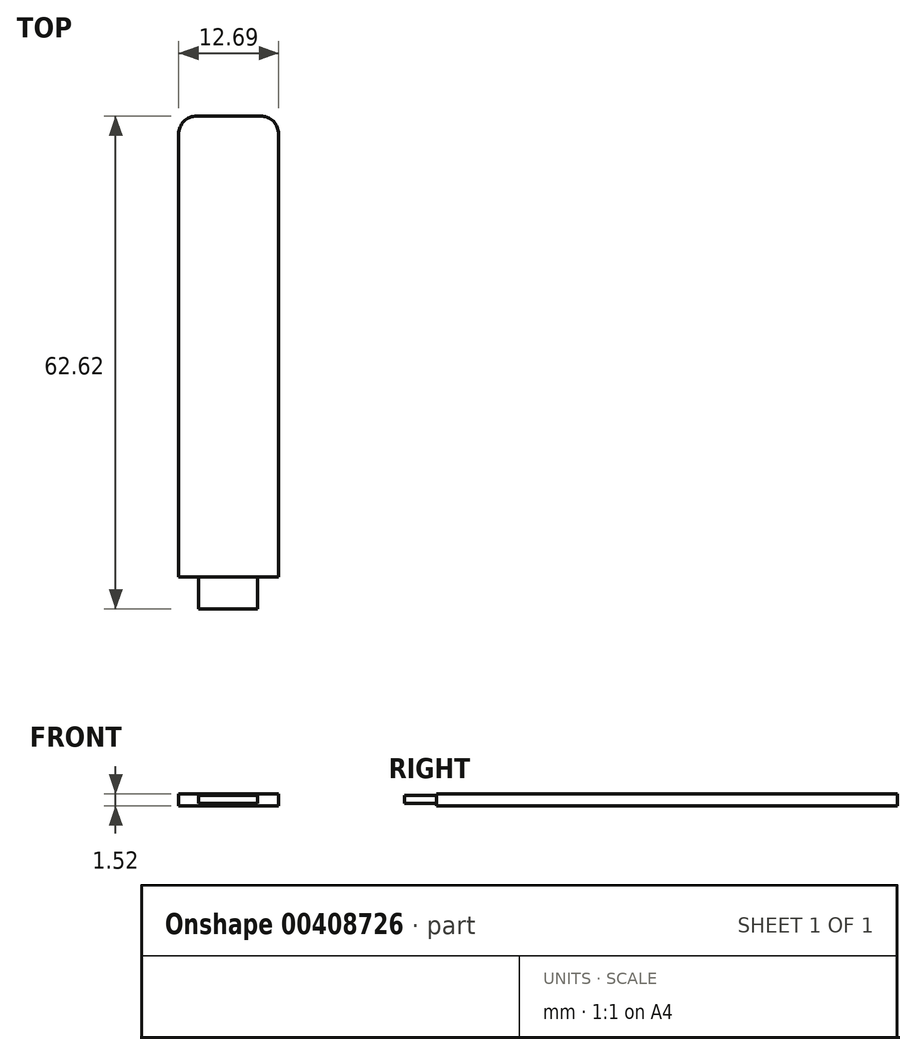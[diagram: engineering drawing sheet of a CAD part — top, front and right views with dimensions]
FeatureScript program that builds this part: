
annotation { "Feature Type Name" : "Feature", "Feature Type Description" : "" }
export const myFeature = defineFeature(function(context is Context, id is Id, definition is map)
    precondition{}
    {
        {
            var Q0;
            Q0=qCreatedBy(makeId("Top.planeOp"),FACE);
            var sketch = newSketch(context, id + "F0", { "sketchPlane" : qUnion([Q0])});
            skLineSegment(sketch, "E0.bottom", {"start": v(-6.25, -9) * mm, "end": v(6.44, -9) * mm});
            skLineSegment(sketch, "E0.top", {"start": v(-6.25, 49.56) * mm, "end": v(6.44, 49.56) * mm});
            skLineSegment(sketch, "E0.left", {"start": v(-6.25, -9) * mm, "end": v(-6.25, 49.56) * mm});
            skLineSegment(sketch, "E0.right", {"start": v(6.44, -9) * mm, "end": v(6.44, 49.56) * mm});
            skLineSegment(sketch, "E1.bottom", {"start": v(-4.3, -9) * mm, "end": v(4.51, -9) * mm});
            skLineSegment(sketch, "E1.top", {"start": v(-4.3, -13.2) * mm, "end": v(4.51, -13.2) * mm});
            skLineSegment(sketch, "E1.left", {"start": v(-4.3, -9) * mm, "end": v(-4.3, -13.2) * mm});
            skLineSegment(sketch, "E1.right", {"start": v(4.51, -9) * mm, "end": v(4.51, -13.2) * mm});
            skSolve(sketch);
        }
        {
            var Q0;
            Q0=makeQuery(id+"F0.imprint","IMPRINT",FACE,{"disambiguationData":[TD([[makeQuery(id+"F0.imprint","IMPRINT",EDGE,{"derivedFrom":sQuery(id+"F0.wireOp",EDGE,"E0.top")}),-1.0]])]});
            extrude(context, id + "F1", {"entities" : qUnion([Q0]), "depth" : 1.52 * mm});
        }
        {
            var Q0;
            Q0=makeQuery(id+"F1.opExtrude","SWEPT_EDGE",EDGE,{"disambiguationData":[OSD([sQuery(id+"F0.wireOp",EDGE,"E0.top"),sQuery(id+"F0.wireOp",EDGE,"E0.left")])]});
            var Q1;
            Q1=makeQuery(id+"F1.opExtrude","SWEPT_EDGE",EDGE,{"disambiguationData":[OSD([sQuery(id+"F0.wireOp",EDGE,"E0.top"),sQuery(id+"F0.wireOp",EDGE,"E0.right")])]});
            fillet(context, id + "F2", {"entities" : qUnion([Q0, Q1]), "radius" : 2.3 * mm, "tangentPropagation" : true, "allowEdgeOverflow" : false});
        }
        {
            var Q0;
            Q0=makeQuery(id+"F1.opExtrude","SWEPT_FACE",FACE,{"disambiguationData":[OSD([sQuery(id+"F0.wireOp",EDGE,"E0.bottom"),sQuery(id+"F0.wireOp",EDGE,"E1.bottom")])]});
            var sketch = newSketch(context, id + "F3", { "sketchPlane" : qUnion([Q0])});
            skLineSegment(sketch, "E2.bottom", {"start": v(3.75, 1.35) * mm, "end": v(-3.75, 1.35) * mm});
            skLineSegment(sketch, "E2.top", {"start": v(3.75, 0.3) * mm, "end": v(-3.75, 0.3) * mm});
            skLineSegment(sketch, "E2.left", {"start": v(3.75, 1.35) * mm, "end": v(3.75, 0.3) * mm});
            skLineSegment(sketch, "E2.right", {"start": v(-3.75, 1.35) * mm, "end": v(-3.75, 0.3) * mm});
            skPoint(sketch, "E2.middle", {"position": v(0, 0.82) * mm});
            skSolve(sketch);
        }
        {
            var Q0;
            Q0=makeQuery(id+"F3.imprint","IMPRINT",FACE,{"disambiguationData":[TD([[makeQuery(id+"F3.imprint","IMPRINT",EDGE,{"derivedFrom":sQuery(id+"F3.wireOp",EDGE,"E2.bottom")}),1.0]])]});
            extrude(context, id + "F4", {"entities" : qUnion([Q0]), "operationType" : NewBodyOperationType.ADD, "depth" : 4.06 * mm});
        }
    });
